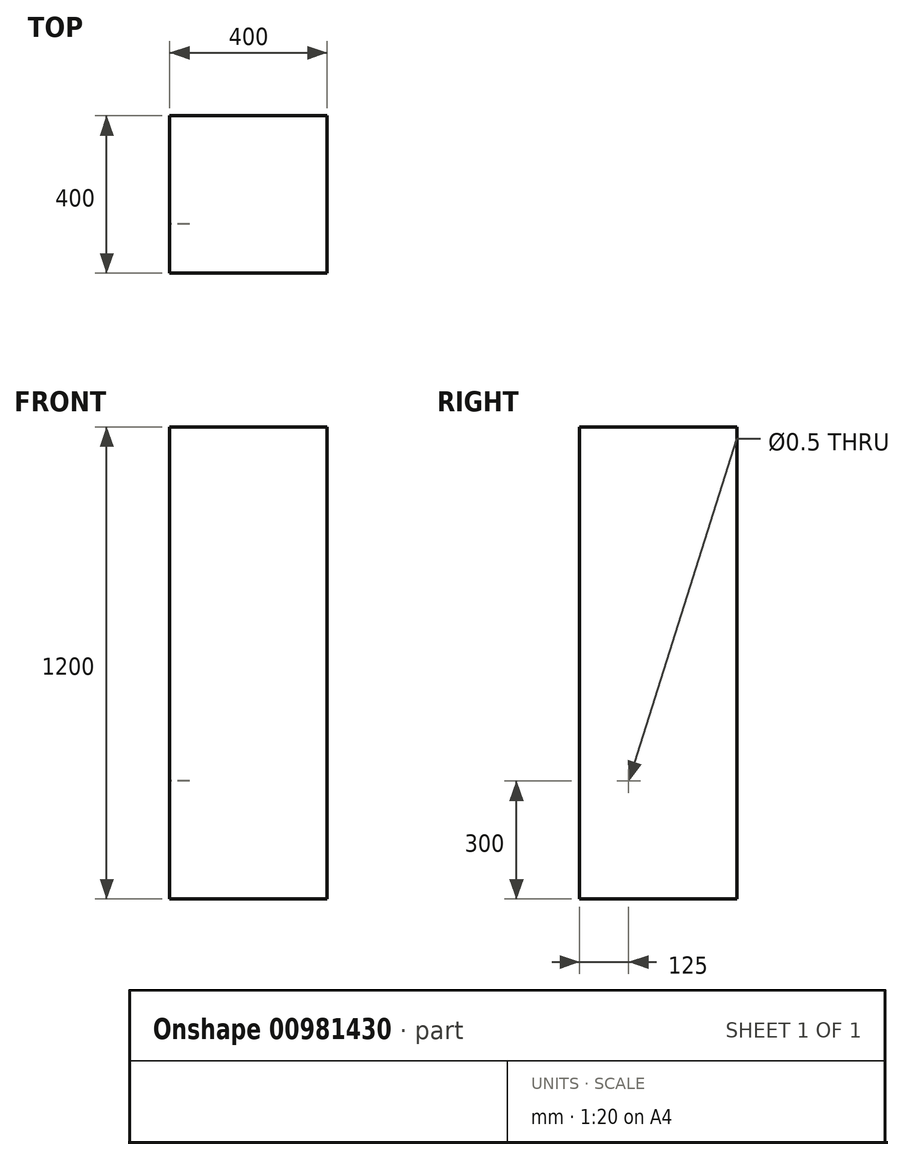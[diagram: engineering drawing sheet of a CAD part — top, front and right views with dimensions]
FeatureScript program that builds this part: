
annotation { "Feature Type Name" : "Feature", "Feature Type Description" : "" }
export const myFeature = defineFeature(function(context is Context, id is Id, definition is map)
    precondition{}
    {
        {
            var Q0;
            Q0=qCreatedBy(makeId("Top.planeOp"),FACE);
            var sketch = newSketch(context, id + "F0", { "sketchPlane" : qUnion([Q0])});
            skLineSegment(sketch, "E0.bottom", {"start": v(-200, 200) * mm, "end": v(200, 200) * mm});
            skLineSegment(sketch, "E0.top", {"start": v(-200, -200) * mm, "end": v(200, -200) * mm});
            skLineSegment(sketch, "E0.left", {"start": v(-200, 200) * mm, "end": v(-200, -200) * mm});
            skLineSegment(sketch, "E0.right", {"start": v(200, 200) * mm, "end": v(200, -200) * mm});
            skPoint(sketch, "E0.middle", {"position": v(0, 0) * mm});
            skSolve(sketch);
        }
        {
            var Q0;
            Q0 = qSketchRegion(id + "F0", true);
            extrude(context, id + "F1", {"entities" : qUnion([Q0]), "depth" : 1200 * mm, "offsetDistance" : 25 * mm});
        }
        {
            var Q0;
            Q0=makeQuery(id+"F1.opExtrude","SWEPT_FACE",FACE,{"disambiguationData":[OSD([sQuery(id+"F0.wireOp",EDGE,"E0.left")])]});
            cPlane(context, id + "F2", {"entities" : qUnion([Q0]), "cplaneType" : CPlaneType.OFFSET, "offset" : 0 * mm, "width" : 150 * mm, "height" : 150 * mm});
        }
        {
            var Q0;
            Q0=qCreatedBy(id+"F2.planeOp",FACE);
            var sketch = newSketch(context, id + "F3", { "sketchPlane" : qUnion([Q0])});
            skPoint(sketch, "E1", {"position": v(75, 300) * mm});
            skSolve(sketch);
        }
        {
            var Q0;
            Q0=sQuery(id+"F3.wireOp",VERTEX,"E1");
            var Q1;
            Q1=makeQuery(id+"F1.opExtrude","SWEPT_BODY",BODY,{"disambiguationData":[OSD([sQuery(id+"F0.wireOp",EDGE,"E0.bottom"),sQuery(id+"F0.wireOp",EDGE,"E0.top"),sQuery(id+"F0.wireOp",EDGE,"E0.left"),sQuery(id+"F0.wireOp",EDGE,"E0.right")])]});
            hole(context, id + "F4", {"style" : HoleStyle.SIMPLE, "endStyle" : HoleEndStyle.BLIND, "holeDiameter" : 0.5 * mm, "majorDiameter" : 5 * mm, "holeDepth" : 50 * mm, "isTappedThrough" : true, "tappedDepth" : 12 * mm, "tapClearance" : 3, "startFromSketch" : true, "locations" : qUnion([Q0]), "scope" : qUnion([Q1])});
        }
    });
